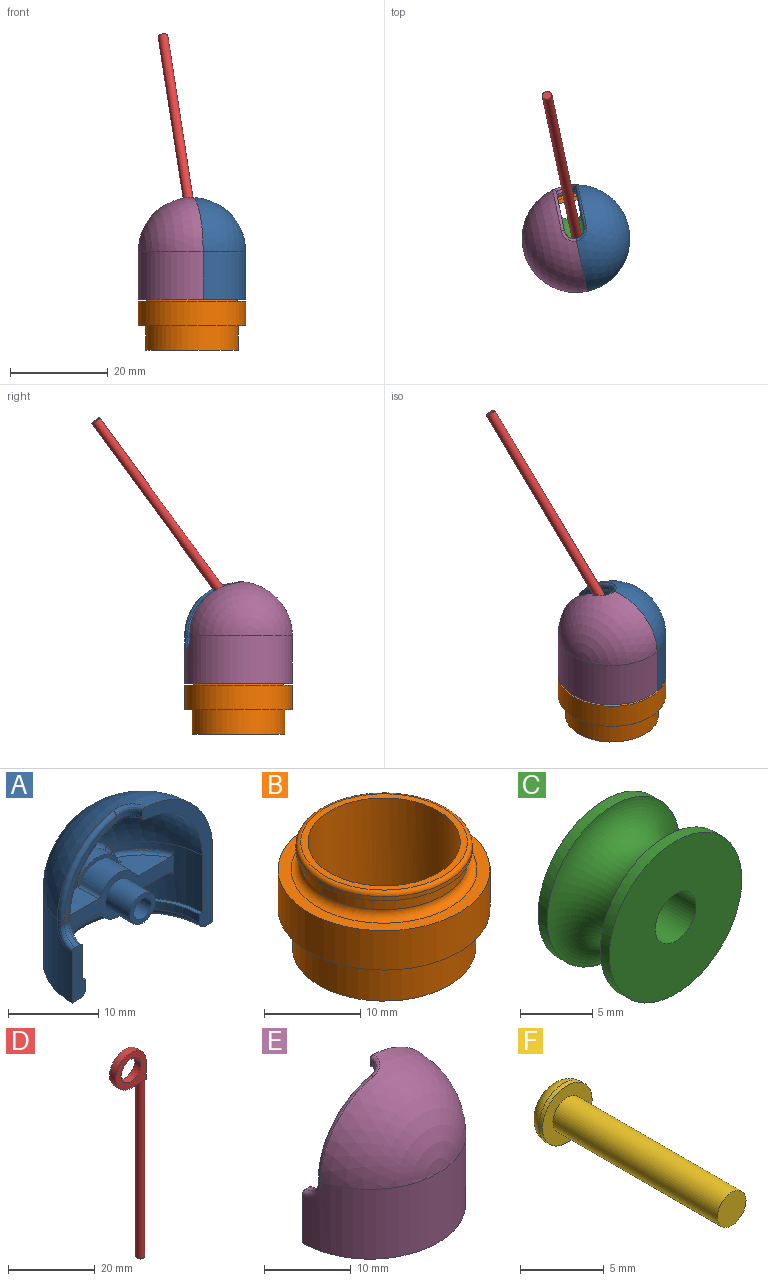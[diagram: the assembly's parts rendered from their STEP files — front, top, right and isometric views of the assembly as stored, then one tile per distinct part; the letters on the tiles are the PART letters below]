
ASSEMBLY  parts=6 mates=5
PART A: 57 faces, bbox 23.1x12x21.3 mm
  f0: cylinder r=3.47mm len=6.44mm, axis (0,-1,0), area 12.2mm2, adj f1,f37,f41,f42,f44,f45
  f1: plane 7.36x2.48mm, normal (0,-1,0), area 4.1mm2, adj f0,f2,f33,f34,f37,f41,f54,f56
  f2: cylinder r=2.98mm len=5.37mm, axis (0,-1,0), area 21.7mm2, adj f1,f36,f54,f56
  f3: cylinder r=9.35mm len=18.7mm, axis (0,0,-1), area 133.8mm2, adj f6,f10,f12,f13,f21,f22,f36,f38
  f4: cylinder r=2.98mm len=5.37mm, axis (0,-1,0), area 21.7mm2, adj f30,f36,f53,f55
  f5: cylinder r=11mm len=22mm, axis (0,0,1), area 312.4mm2, adj f6,f7,f8,f13,f16,f27,f28
  f6: plane 7.32x2.17mm, normal (0,-1,0), area 12.8mm2, adj f3,f5,f7,f11,f12,f18,f21,f28
  f7: plane 22x11mm, normal (0,0,-1), area 37.7mm2, adj f5,f6,f13,f31
  f8: sphere r=11mm, area 335mm2, adj f5,f13,f25,f26
  f9: cylinder r=1.98mm len=3.95mm, axis (0,-1,0), area 46.5mm2, adj f14,f36
  f10: sphere r=9.35mm, area 232.7mm2, adj f3,f13,f23,f24,f44
  f11: cylinder r=8.85mm len=17.7mm, axis (0,0,-1), area 30.6mm2, adj f6,f12,f13,f31
  f12: plane 18.7x9.35mm, normal (0,0,1), area 14.3mm2, adj f3,f6,f11,f13
  f13: plane 20.81x11.02mm, normal (0,-1,0), area 43.3mm2, adj f3,f5,f7,f8,f10,f11,f12,f19
  f14: plane 3.95x3.95mm, normal (0,-1,0), area 6.5mm2, adj f9,f20
  f15: plane 5x5mm, normal (0,1,0), area 13.9mm2, adj f16,f20
  f16: cylinder r=2.5mm len=5mm, axis (0,1,0), area 44.9mm2, adj f5,f15
  f17: plane 10.5x8.2mm, normal (0,-1,0), area 9.4mm2, adj f18,f19,f22,f23,f26,f27
  f18: cylinder r=2mm len=2mm, axis (-1,0,0), area 2.1mm2, adj f6,f17,f21,f28
  f19: cylinder r=2mm len=2mm, axis (0,0,-1), area 2.1mm2, adj f13,f17,f24,f25
  f20: cylinder r=1.35mm len=8mm, axis (0,1,0), area 67.9mm2, adj f14,f15
  f21: bspline ~3.05x2.74mm, area 2.5mm2, adj f3,f6,f18,f22
  f22: cylinder r=0.5mm len=0.5mm, axis (0,0,-1), area 0.3mm2, adj f3,f17,f21,f23
  f23: torus R=9.53mm, axis (0,-1,0), area 8.3mm2, adj f10,f17,f22,f24
  f24: bspline ~2.93x2.82mm, area 2.4mm2, adj f10,f13,f19,f23
  f25: bspline ~3.11x2.77mm, area 3mm2, adj f8,f13,f19,f26
  f26: torus R=10.2mm, axis (0,-1,0), area 13.1mm2, adj f8,f17,f25,f27
  f27: cylinder r=0.5mm len=0.62mm, axis (0,0,1), area 0.5mm2, adj f5,f17,f26,f28
  f28: bspline ~3.05x3.03mm, area 2.9mm2, adj f5,f6,f18,f27
  f29: cylinder r=3.47mm len=6.44mm, axis (0,-1,0), area 12.6mm2, adj f30,f47,f48,f52
  f30: plane 7.36x2.48mm, normal (0,-1,0), area 4.1mm2, adj f4,f29,f32,f35,f47,f48,f53,f55
  f31: torus R=9.85mm, axis (0,0,1), area 45.5mm2, adj f6,f7,f11,f13
  f32: plane 4.88x4.3mm, normal (0,0,-1), area 13.3mm2, adj f30,f36,f48,f49,f53
  f33: plane 4.88x4.3mm, normal (0,0,1), area 13.3mm2, adj f1,f36,f40,f41,f54
  f34: plane 4.88x4.3mm, normal (0,0,1), area 13.3mm2, adj f1,f36,f37,f38,f56
  f35: plane 4.88x4.3mm, normal (0,0,-1), area 13.3mm2, adj f30,f36,f46,f47,f55
  f36: plane 17.23x6.05mm, normal (0,-1,0), area 38.4mm2, adj f2,f3,f4,f9,f32,f33,f34,f35
  f37: cylinder r=0.5mm len=1.05mm, axis (0,-1,0), area 0.6mm2, adj f0,f1,f34,f39
  f38: torus R=8.85mm, axis (0,0,-1), area 5.2mm2, adj f3,f34,f36,f39
  f39: sphere r=0.5mm, area 0.5mm2, adj f37,f38,f42
  f40: torus R=8.85mm, axis (0,0,-1), area 5.2mm2, adj f3,f33,f36,f43
  f41: cylinder r=0.5mm len=1.05mm, axis (0,-1,0), area 0.6mm2, adj f0,f1,f33,f43
  f42: bspline ~1.67x1.44mm, area 1mm2, adj f0,f3,f39,f44
  f43: sphere r=0.5mm, area 0.5mm2, adj f40,f41,f45
  f44: bspline ~7.58x2.72mm, area 6.1mm2, adj f0,f10,f42,f45
  f45: bspline ~1.67x1.44mm, area 1mm2, adj f0,f3,f43,f44
  f46: torus R=8.85mm, axis (0,0,-1), area 5.2mm2, adj f3,f35,f36,f50
  f47: cylinder r=0.5mm len=1.05mm, axis (0,-1,0), area 0.6mm2, adj f29,f30,f35,f50
  f48: cylinder r=0.5mm len=1.05mm, axis (0,-1,0), area 0.6mm2, adj f29,f30,f32,f51
  f49: torus R=8.85mm, axis (0,0,-1), area 5.2mm2, adj f3,f32,f36,f51
  f50: sphere r=0.5mm, area 0.4mm2, adj f46,f47,f52
  f51: sphere r=0.5mm, area 0.5mm2, adj f48,f49,f52
  f52: bspline ~8.17x3.32mm, area 7.8mm2, adj f3,f29,f50,f51
  f53: cylinder r=0.5mm len=3.25mm, axis (0,-1,0), area 1.8mm2, adj f4,f30,f32,f36
  f54: cylinder r=0.5mm len=3.25mm, axis (0,-1,0), area 1.8mm2, adj f1,f2,f33,f36
  f55: cylinder r=0.5mm len=3.25mm, axis (0,-1,0), area 1.8mm2, adj f4,f30,f35,f36
  f56: cylinder r=0.5mm len=3.25mm, axis (0,-1,0), area 1.8mm2, adj f1,f2,f34,f36
PART B: 12 faces, bbox 22.4x22.4x13.5 mm
  f0: cylinder r=7.9mm len=15.8mm, axis (0,0,-1), area 670.1mm2, adj f6,f9
  f1: cylinder r=9.15mm len=18.3mm, axis (0,0,-1), area 28.7mm2, adj f8,f10
  f2: cylinder r=11mm len=22mm, axis (0,0,-1), area 345.6mm2, adj f3,f4
  f3: plane 22x22mm, normal (0,0,1), area 87.6mm2, adj f2,f11
  f4: plane 22x22mm, normal (0,0,-1), area 96.6mm2, adj f2,f5
  f5: cylinder r=9.5mm len=19mm, axis (0,0,1), area 298.5mm2, adj f4,f6
  f6: plane 19x19mm, normal (0,0,-1), area 87.5mm2, adj f0,f5
  f7: cylinder r=8.65mm len=17.3mm, axis (0,0,-1), area 81.5mm2, adj f8,f11
  f8: plane 18.3x18.3mm, normal (0,0,-1), area 28mm2, adj f1,f7
  f9: plane 17.3x17.3mm, normal (0,0,1), area 39mm2, adj f0,f10
  f10: torus R=8.65mm, axis (0,0,1), area 44.3mm2, adj f1,f9
  f11: torus R=9.65mm, axis (0,0,1), area 89mm2, adj f3,f7
PART C: 6 faces, bbox 18.1x7x18.1 mm
  f0: cylinder r=6.5mm len=13mm, axis (0,1,0), area 36.8mm2, adj f4,f5
  f1: cylinder r=6.5mm len=13mm, axis (0,1,0), area 36.8mm2, adj f3,f5
  f2: cylinder r=2mm len=7mm, axis (0,1,0), area 88mm2, adj f3,f4
  f3: plane 13x13mm, normal (0,-1,0), area 120.2mm2, adj f1,f2
  f4: plane 13x13mm, normal (0,1,0), area 120.2mm2, adj f0,f2
  f5: torus R=6.5mm, axis (0,1,0), area 248.6mm2, adj f0,f1
PART D: 10 faces, bbox 10x2x60 mm
  f0: cylinder r=1mm len=50mm, axis (0,0,-1), area 314.2mm2, adj f1,f2,f3,f4
  f1: plane 2x2mm, normal (0,0,-1), area 3.1mm2, adj f0
  f2: plane 1x1mm, normal (0,0,-1), area 0.2mm2, adj f0,f6,f7
  f3: plane 4x2mm, normal (0,0,-1), area 6.4mm2, adj f0,f5,f7,f8
  f4: plane 1x1mm, normal (0,0,-1), area 0.2mm2, adj f0,f5,f6
  f5: plane 10x10mm, normal (0,-1,0), area 52.4mm2, adj f3,f4,f6,f8,f9
  f6: plane 5x2mm, normal (1,0,0), area 10mm2, adj f2,f4,f5,f7,f8
  f7: plane 10x10mm, normal (0,1,0), area 52.4mm2, adj f2,f3,f6,f8,f9
  f8: cylinder r=5mm len=10mm, axis (0,-1,0), area 47.1mm2, adj f3,f5,f6,f7
  f9: cylinder r=3.17mm len=6.33mm, axis (0,1,0), area 39.8mm2, adj f5,f7
PART E: 49 faces, bbox 23.1x12x21.3 mm
  f0: cylinder r=9.35mm len=18.7mm, axis (0,0,-1), area 139.8mm2, adj f3,f6,f8,f10,f14,f20,f21,f33
  f1: cylinder r=2.98mm len=5.37mm, axis (0,1,0), area 30.3mm2, adj f14,f43,f44,f48
  f2: cylinder r=11mm len=22mm, axis (0,0,1), area 332.2mm2, adj f3,f4,f5,f10,f26,f27
  f3: plane 7.32x2.17mm, normal (0,1,0), area 12.8mm2, adj f0,f2,f4,f7,f8,f13,f20,f27
  f4: plane 22x11mm, normal (0,0,-1), area 37.7mm2, adj f2,f3,f10,f28
  f5: sphere r=11mm, area 335mm2, adj f2,f10,f24,f25
  f6: sphere r=9.35mm, area 236.2mm2, adj f0,f10,f22,f23,f39
  f7: cylinder r=8.85mm len=17.7mm, axis (0,0,-1), area 30.6mm2, adj f3,f8,f10,f28
  f8: plane 18.7x9.35mm, normal (0,0,1), area 14.3mm2, adj f0,f3,f7,f10
  f9: cylinder r=2.98mm len=5.37mm, axis (0,1,0), area 31.6mm2, adj f14,f34,f36,f37,f39,f41
  f10: plane 20.81x11.02mm, normal (0,1,0), area 43.3mm2, adj f0,f2,f4,f5,f6,f7,f8,f12
  f11: plane 10.5x8.2mm, normal (0,1,0), area 9.4mm2, adj f12,f13,f21,f22,f25,f26
  f12: cylinder r=2mm len=2mm, axis (0,0,1), area 2.1mm2, adj f10,f11,f23,f24
  f13: cylinder r=2mm len=2mm, axis (1,0,0), area 2.1mm2, adj f3,f11,f20,f27
  f14: plane 17.23x6.05mm, normal (0,1,0), area 38.4mm2, adj f0,f1,f9,f18,f29,f30,f31,f32
  f15: plane 2x2mm, normal (0,1,0), area 3.1mm2, adj f16
  f16: cylinder r=1mm len=6.65mm, axis (0,1,0), area 41.8mm2, adj f15,f19
  f17: plane 3.95x3.95mm, normal (0,1,0), area 6.5mm2, adj f18,f19
  f18: cylinder r=1.98mm len=3.95mm, axis (0,1,0), area 46.5mm2, adj f14,f17
  f19: cone r=1.35mm half-angle=45deg, axis (0,1,0), area 3.7mm2, adj f16,f17
  f20: bspline ~2.74x2.64mm, area 2.5mm2, adj f0,f3,f13,f21
  f21: cylinder r=0.5mm len=0.5mm, axis (0,0,-1), area 0.3mm2, adj f0,f11,f20,f22
  f22: torus R=9.53mm, axis (0,-1,0), area 8.3mm2, adj f6,f11,f21,f23
  f23: bspline ~2.93x2.82mm, area 2.4mm2, adj f6,f10,f12,f22
  f24: bspline ~3.22x3.11mm, area 3mm2, adj f5,f10,f12,f25
  f25: torus R=10.2mm, axis (0,-1,0), area 13.1mm2, adj f5,f11,f24,f26
  f26: cylinder r=0.5mm len=0.62mm, axis (0,0,1), area 0.5mm2, adj f2,f11,f25,f27
  f27: bspline ~3.05x3.03mm, area 2.9mm2, adj f2,f3,f13,f26
  f28: torus R=9.85mm, axis (0,0,1), area 45.5mm2, adj f3,f4,f7,f10
  f29: plane 4.88x4.53mm, normal (0,0,-1), area 14mm2, adj f14,f44,f45
  f30: plane 4.88x4.53mm, normal (0,0,1), area 14mm2, adj f14,f33,f34
  f31: plane 4.88x4.53mm, normal (0,0,1), area 14mm2, adj f14,f37,f38
  f32: plane 4.88x4.53mm, normal (0,0,-1), area 14mm2, adj f14,f42,f43
  f33: torus R=8.85mm, axis (0,0,1), area 5.6mm2, adj f0,f14,f30,f35
  f34: cylinder r=0.5mm len=4.53mm, axis (0,1,0), area 2.5mm2, adj f9,f14,f30,f35
  f35: sphere r=0.5mm, area 0.3mm2, adj f33,f34,f36
  f36: bspline ~1.95x1.58mm, area 1.1mm2, adj f0,f9,f35,f39
  f37: cylinder r=0.5mm len=4.53mm, axis (0,1,0), area 2.5mm2, adj f9,f14,f31,f40
  f38: torus R=8.85mm, axis (0,0,1), area 5.6mm2, adj f0,f14,f31,f40
  f39: bspline ~6.18x2.05mm, area 4.3mm2, adj f6,f9,f36,f41
  f40: sphere r=0.5mm, area 0.4mm2, adj f37,f38,f41
  f41: bspline ~1.95x1.58mm, area 1.1mm2, adj f0,f9,f39,f40
  f42: torus R=8.85mm, axis (0,0,1), area 5.6mm2, adj f0,f14,f32,f46
  f43: cylinder r=0.5mm len=4.53mm, axis (0,1,0), area 2.5mm2, adj f1,f14,f32,f46
  f44: cylinder r=0.5mm len=4.53mm, axis (0,1,0), area 2.5mm2, adj f1,f14,f29,f47
  f45: torus R=8.85mm, axis (0,0,1), area 5.6mm2, adj f0,f14,f29,f47
  f46: sphere r=0.5mm, area 0.4mm2, adj f42,f43,f48
  f47: sphere r=0.5mm, area 0.4mm2, adj f44,f45,f48
  f48: bspline ~7.1x2.81mm, area 6.3mm2, adj f0,f1,f46,f47
PART F: 6 faces, bbox 4.5x15.2x4.5 mm
  f0: cylinder r=2.1mm len=4.2mm, axis (0,-1,0), area 4mm2, adj f2,f3
  f1: plane 2.2x2.2mm, normal (0,1,0), area 3.8mm2, adj f3
  f2: plane 4.2x4.2mm, normal (0,-1,0), area 9.2mm2, adj f0,f4
  f3: torus R=1.1mm, axis (0,1,0), area 17.1mm2, adj f0,f1
  f4: cylinder r=1.21mm len=13.9mm, axis (0,1,0), area 106.1mm2, adj f2,f5
  f5: plane 2.43x2.43mm, normal (0,-1,0), area 4.6mm2, adj f4
PLACE A rot(axis=(0,0,-1),78.1deg) t=(34.51,16.76,-60.3)mm
PLACE B t=(34.51,16.76,-60.5)mm fixed
PLACE C rot(axis=(0,0,-1),78.1deg) t=(34.75,16.81,-60.3)mm
PLACE D rot(axis=(0.75,-0.61,0.25),157deg) t=(28.59,45.95,-1.39)mm
PLACE E rot(axis=(0,0,-1),78.1deg) t=(34.51,16.76,-60.3)mm
PLACE F rot(axis=(0,0,-1),78.1deg) t=(34.51,16.76,-60.3)mm
MATE fastened E.f3 <-> A.f6  axis (0.98,0.21,0) through (32.42,26.65,-51.63)mm
MATE revolute D.f9 <-> C.f0  axis (-0.98,-0.21,0) through (34.75,16.81,-47.8)mm
MATE revolute C.f0 <-> A.f0  axis (0.98,0.21,0) through (38.17,17.54,-47.8)mm
MATE fastened F.f0 <-> A.f20  axis (0.98,0.21,0) through (42.33,18.41,-47.8)mm
MATE revolute E.f0 <-> B.f0  axis (0,0,1) through (34.51,16.76,-53)mm
